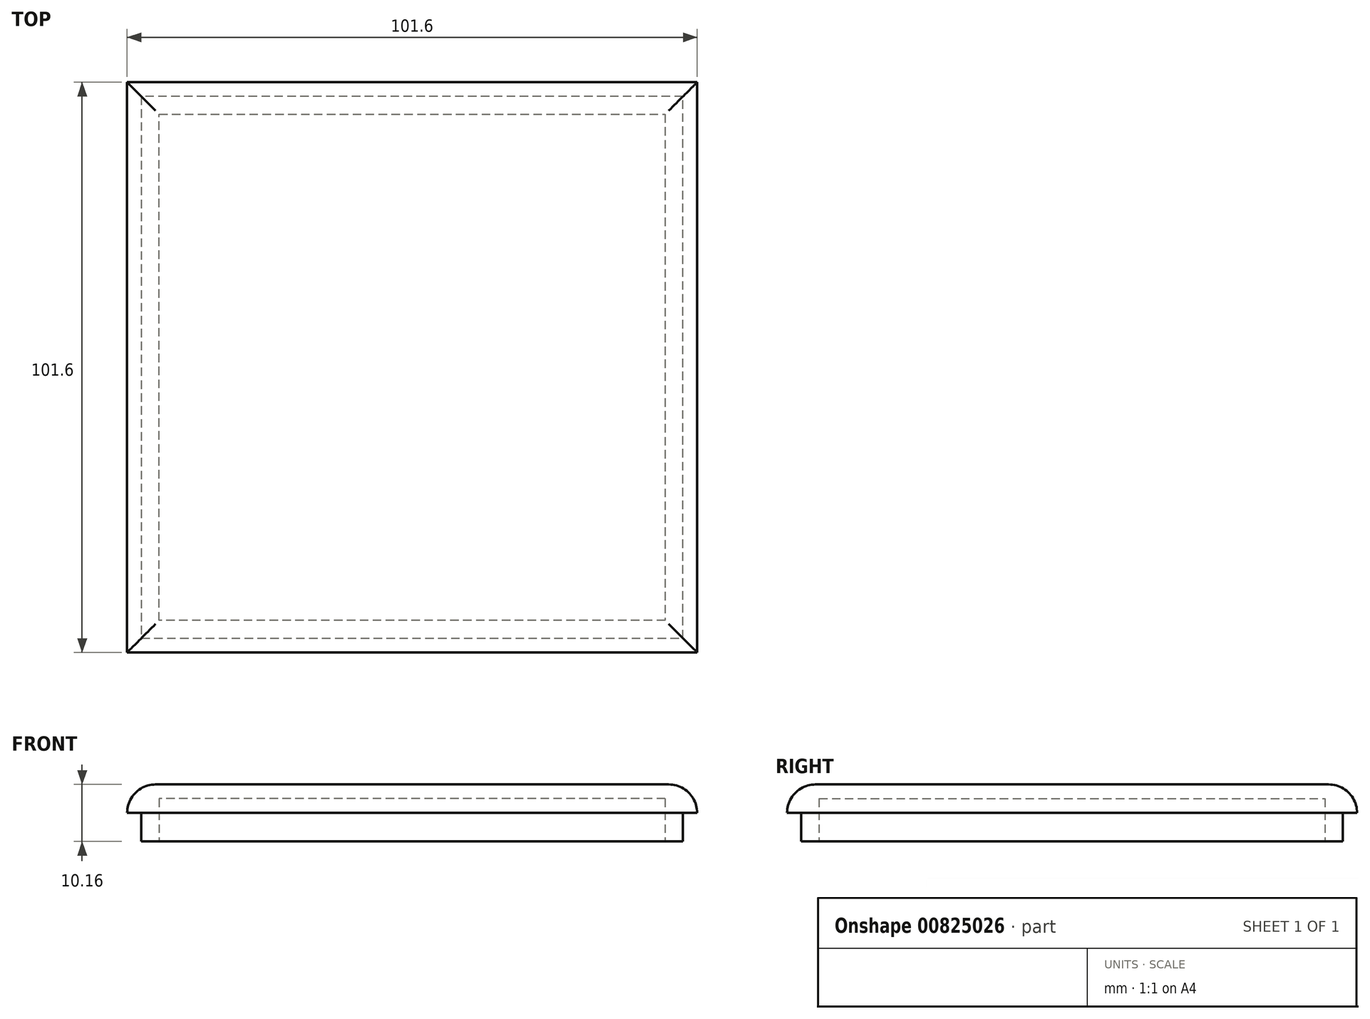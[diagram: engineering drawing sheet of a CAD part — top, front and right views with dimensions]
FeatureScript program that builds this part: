
annotation { "Feature Type Name" : "Feature", "Feature Type Description" : "" }
export const myFeature = defineFeature(function(context is Context, id is Id, definition is map)
    precondition{}
    {
        {
            var Q0;
            Q0=qCreatedBy(makeId("Top.planeOp"),FACE);
            var sketch = newSketch(context, id + "F0", { "sketchPlane" : qUnion([Q0])});
            skLineSegment(sketch, "E0.0", {"start": v(-97, 67) * mm, "end": v(-97, -34.6) * mm});
            skLineSegment(sketch, "E1.0", {"start": v(4.6, 67) * mm, "end": v(-97, 67) * mm});
            skLineSegment(sketch, "E2.0", {"start": v(4.6, -34.6) * mm, "end": v(4.6, 67) * mm});
            skLineSegment(sketch, "E3.0", {"start": v(-97, -34.6) * mm, "end": v(4.6, -34.6) * mm});
            skLineSegment(sketch, "E4.0", {"start": v(-94.46, 64.45) * mm, "end": v(-94.46, -32.07) * mm});
            skLineSegment(sketch, "E5.0", {"start": v(2.06, 64.45) * mm, "end": v(-94.46, 64.45) * mm});
            skLineSegment(sketch, "E6.0", {"start": v(2.06, -32.07) * mm, "end": v(2.06, 64.45) * mm});
            skLineSegment(sketch, "E7.0", {"start": v(-94.46, -32.07) * mm, "end": v(2.06, -32.07) * mm});
            skLineSegment(sketch, "E8", {"start": v(-46.2, 64.45) * mm, "end": v(-46.2, -32.07) * mm, "construction": true});
            skLineSegment(sketch, "E9", {"start": v(-94.46, 16.2) * mm, "end": v(2.06, 16.2) * mm, "construction": true});
            skSolve(sketch);
        }
        {
            var Q0;
            Q0 = qSketchRegion(id + "F0", true);
            var Q1;
            Q1=makeQuery(id+"F0.imprint","IMPRINT",FACE,{"disambiguationData":[TD([[makeQuery(id+"F0.imprint","IMPRINT",EDGE,{"derivedFrom":sQuery(id+"F0.wireOp",EDGE,"E4.0")}),1.0]])]});
            extrude(context, id + "F1", {"entities" : qUnion([Q0, Q1]), "depth" : 5.08 * mm, "offsetDistance" : 25.4 * mm});
        }
        {
            var Q0;
            Q0=makeQuery(id+"F1.opExtrude","CAP_EDGE",EDGE,{"disambiguationData":[OSD([sQuery(id+"F0.wireOp",EDGE,"E0.0")])],"isStart":false});
            var Q1;
            Q1=makeQuery(id+"F1.opExtrude","CAP_EDGE",EDGE,{"disambiguationData":[OSD([sQuery(id+"F0.wireOp",EDGE,"E3.0")])],"isStart":false});
            var Q2;
            Q2=makeQuery(id+"F1.opExtrude","CAP_EDGE",EDGE,{"disambiguationData":[OSD([sQuery(id+"F0.wireOp",EDGE,"E2.0")])],"isStart":false});
            var Q3;
            Q3=makeQuery(id+"F1.opExtrude","CAP_EDGE",EDGE,{"disambiguationData":[OSD([sQuery(id+"F0.wireOp",EDGE,"E1.0")])],"isStart":false});
            fillet(context, id + "F2", {"entities" : qUnion([Q0, Q1, Q2, Q3]), "radius" : 5.08 * mm, "tangentPropagation" : true, "allowEdgeOverflow" : false});
        }
        {
            var Q0;
            Q0=makeQuery(id+"F0.imprint","IMPRINT",FACE,{"disambiguationData":[TD([[makeQuery(id+"F0.imprint","IMPRINT",EDGE,{"derivedFrom":sQuery(id+"F0.wireOp",EDGE,"E4.0")}),1.0]])]});
            extrude(context, id + "F3", {"entities" : qUnion([Q0]), "operationType" : NewBodyOperationType.ADD, "oppositeDirection" : true, "depth" : 5.08 * mm, "offsetDistance" : 25.4 * mm});
        }
        {
            var Q0;
            Q0=makeQuery(id+"F3.opExtrude","CAP_FACE",FACE,{"disambiguationData":[OSD([sQuery(id+"F0.wireOp",EDGE,"E4.0"),sQuery(id+"F0.wireOp",EDGE,"E5.0"),sQuery(id+"F0.wireOp",EDGE,"E6.0"),sQuery(id+"F0.wireOp",EDGE,"E7.0")])],"isStart":false});
            var sketch = newSketch(context, id + "F4", { "sketchPlane" : qUnion([Q0])});
            skLineSegment(sketch, "E10.0", {"start": v(-91.29, 28.9) * mm, "end": v(-91.29, -61.28) * mm});
            skLineSegment(sketch, "E10.1", {"start": v(-1.12, 28.9) * mm, "end": v(-91.29, 28.9) * mm});
            skLineSegment(sketch, "E10.2", {"start": v(-1.12, -61.28) * mm, "end": v(-1.12, 28.9) * mm});
            skLineSegment(sketch, "E10.3", {"start": v(-91.29, -61.28) * mm, "end": v(-1.12, -61.28) * mm});
            skSolve(sketch);
        }
        {
            var Q0;
            Q0=makeQuery(id+"F4.imprint","IMPRINT",FACE,{"disambiguationData":[TD([[makeQuery(id+"F4.imprint","IMPRINT",EDGE,{"derivedFrom":sQuery(id+"F4.wireOp",EDGE,"E10.0")}),1.0]])]});
            extrude(context, id + "F5", {"entities" : qUnion([Q0]), "operationType" : NewBodyOperationType.REMOVE, "oppositeDirection" : true, "depth" : 7.62 * mm, "offsetDistance" : 25.4 * mm});
        }
    });
